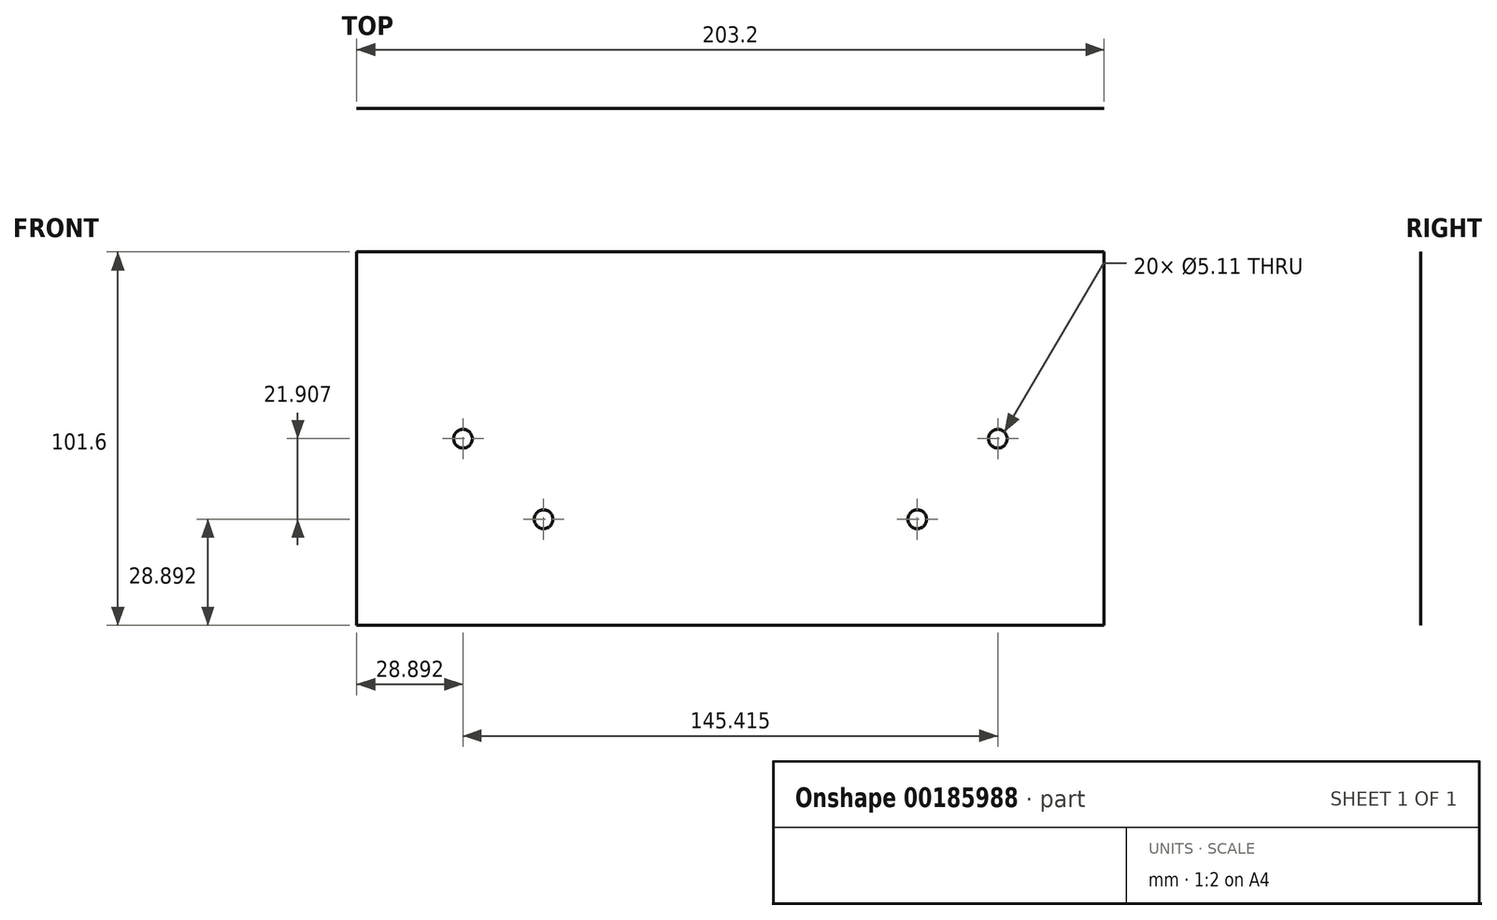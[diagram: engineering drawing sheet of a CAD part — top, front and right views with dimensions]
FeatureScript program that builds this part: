
annotation { "Feature Type Name" : "Feature", "Feature Type Description" : "" }
export const myFeature = defineFeature(function(context is Context, id is Id, definition is map)
    precondition{}
    {
        {
            var Q0;
            Q0=qCreatedBy(makeId("Front.planeOp"),FACE);
            var sketch = newSketch(context, id + "F0", { "sketchPlane" : qUnion([Q0])});
            skLineSegment(sketch, "E0.bottom", {"start": v(101.6, -50.8) * mm, "end": v(-101.6, -50.8) * mm});
            skLineSegment(sketch, "E0.top", {"start": v(101.6, 50.8) * mm, "end": v(-101.6, 50.8) * mm});
            skLineSegment(sketch, "E0.left", {"start": v(101.6, -50.8) * mm, "end": v(101.6, 50.8) * mm});
            skLineSegment(sketch, "E0.right", {"start": v(-101.6, -50.8) * mm, "end": v(-101.6, 50.8) * mm});
            skPoint(sketch, "E0.middle", {"position": v(0, 0) * mm});
            skSolve(sketch);
        }
        {
            var Q0;
            Q0 = qSketchRegion(id + "F0", true);
            extrude(context, id + "F1", {"entities" : qUnion([Q0]), "depth" : 1 / 203.2 * mm});
        }
        {
            var Q0;
            Q0=makeQuery(id+"F1.opExtrude","CAP_FACE",FACE,{"disambiguationData":[OSD([sQuery(id+"F0.wireOp",EDGE,"E0.bottom"),sQuery(id+"F0.wireOp",EDGE,"E0.top"),sQuery(id+"F0.wireOp",EDGE,"E0.left"),sQuery(id+"F0.wireOp",EDGE,"E0.right")])],"isStart":false});
            var sketch = newSketch(context, id + "F2", { "sketchPlane" : qUnion([Q0])});
            skPoint(sketch, "E1", {"position": v(-50.8, -21.9) * mm});
            skPoint(sketch, "E2", {"position": v(50.8, -21.9) * mm});
            skPoint(sketch, "E3", {"position": v(-72.7, 0) * mm});
            skPoint(sketch, "E4", {"position": v(72.7, 0) * mm});
            skSolve(sketch);
        }
        {
            var Q0;
            Q0=sQuery(id+"F2.wireOp",VERTEX,"E1");
            var Q1;
            Q1=sQuery(id+"F2.wireOp",VERTEX,"E2");
            var Q2;
            Q2=sQuery(id+"F2.wireOp",VERTEX,"E3");
            var Q3;
            Q3=sQuery(id+"F2.wireOp",VERTEX,"E4");
            var Q4;
            Q4=makeQuery(id+"F1.opExtrude","SWEPT_BODY",BODY,{"disambiguationData":[OSD([sQuery(id+"F0.wireOp",EDGE,"E0.bottom"),sQuery(id+"F0.wireOp",EDGE,"E0.top"),sQuery(id+"F0.wireOp",EDGE,"E0.left"),sQuery(id+"F0.wireOp",EDGE,"E0.right")])]});
            hole(context, id + "F3", {"style" : HoleStyle.SIMPLE, "endStyle" : HoleEndStyle.BLIND, "standardTappedOrClearance" : lookupTablePath({ "standard" : "ANSI", "fit" : "Normal (ASME)", "size" : "#10", "type" : "Clearance" }), "standardBlindInLast" : lookupTablePath({ "fit" : "Free", "standard" : "ANSI", "size" : "#10", "type" : "Clearance" }), "holeDiameter" : 5.1 * mm, "holeDepth" : 25 * mm, "locations" : qUnion([Q0, Q1, Q2, Q3]), "scope" : qUnion([Q4])});
        }
    });
